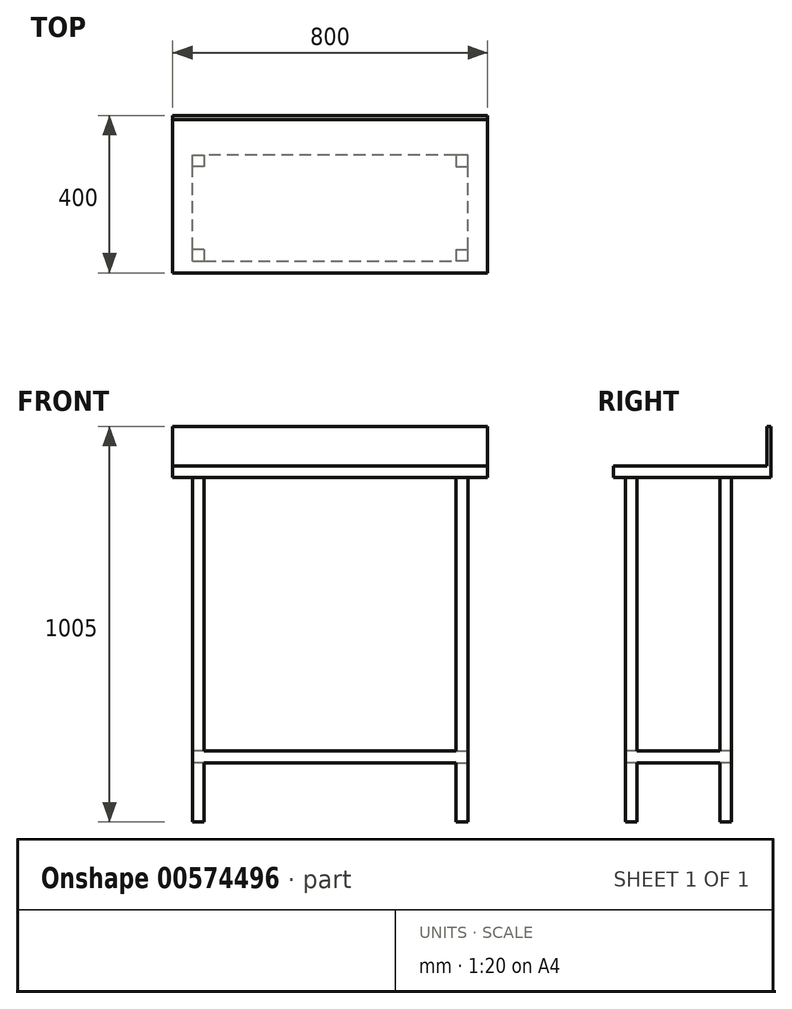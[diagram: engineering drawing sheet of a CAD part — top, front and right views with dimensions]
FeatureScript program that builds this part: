
annotation { "Feature Type Name" : "Feature", "Feature Type Description" : "" }
export const myFeature = defineFeature(function(context is Context, id is Id, definition is map)
    precondition{}
    {
        {
            var Q0;
            Q0=qCreatedBy(makeId("Top.planeOp"),FACE);
            var sketch = newSketch(context, id + "F0", { "sketchPlane" : qUnion([Q0])});
            skLineSegment(sketch, "E0.bottom", {"start": v(400, 200) * mm, "end": v(-400, 200) * mm});
            skLineSegment(sketch, "E0.top", {"start": v(400, -200) * mm, "end": v(-400, -200) * mm});
            skLineSegment(sketch, "E0.left", {"start": v(400, 200) * mm, "end": v(400, -200) * mm});
            skLineSegment(sketch, "E0.right", {"start": v(-400, 200) * mm, "end": v(-400, -200) * mm});
            skPoint(sketch, "E0.middle", {"position": v(0, 0) * mm});
            skSolve(sketch);
        }
        {
            var Q0;
            Q0 = qSketchRegion(id + "F0", true);
            extrude(context, id + "F1", {"entities" : qUnion([Q0]), "depth" : 30 * mm, "offsetDistance" : 25 * mm});
        }
        {
            var Q0;
            Q0=makeQuery(id+"F1.opExtrude","CAP_FACE",FACE,{"disambiguationData":[OSD([sQuery(id+"F0.wireOp",EDGE,"E0.bottom"),sQuery(id+"F0.wireOp",EDGE,"E0.top"),sQuery(id+"F0.wireOp",EDGE,"E0.left"),sQuery(id+"F0.wireOp",EDGE,"E0.right")])],"isStart":false});
            var sketch = newSketch(context, id + "F2", { "sketchPlane" : qUnion([Q0])});
            skLineSegment(sketch, "E1.bottom", {"start": v(-400, 200) * mm, "end": v(400, 200) * mm});
            skLineSegment(sketch, "E1.top", {"start": v(-400, 190) * mm, "end": v(400, 190) * mm});
            skLineSegment(sketch, "E1.left", {"start": v(-400, 200) * mm, "end": v(-400, 190) * mm});
            skLineSegment(sketch, "E1.right", {"start": v(400, 200) * mm, "end": v(400, 190) * mm});
            skSolve(sketch);
        }
        {
            var Q0;
            Q0 = qSketchRegion(id + "F2", true);
            extrude(context, id + "F3", {"entities" : qUnion([Q0]), "operationType" : NewBodyOperationType.ADD, "depth" : 100 * mm, "offsetDistance" : 25 * mm});
        }
        {
            var Q0;
            Q0=makeQuery(id+"F1.opExtrude","CAP_FACE",FACE,{"disambiguationData":[OSD([sQuery(id+"F0.wireOp",EDGE,"E0.bottom"),sQuery(id+"F0.wireOp",EDGE,"E0.top"),sQuery(id+"F0.wireOp",EDGE,"E0.left"),sQuery(id+"F0.wireOp",EDGE,"E0.right")])],"isStart":true});
            var sketch = newSketch(context, id + "F4", { "sketchPlane" : qUnion([Q0])});
            skLineSegment(sketch, "E2.bottom", {"start": v(350, 170) * mm, "end": v(320, 170) * mm});
            skLineSegment(sketch, "E2.top", {"start": v(350, 140) * mm, "end": v(320, 140) * mm});
            skLineSegment(sketch, "E2.left", {"start": v(350, 170) * mm, "end": v(350, 140) * mm});
            skLineSegment(sketch, "E2.right", {"start": v(320, 170) * mm, "end": v(320, 140) * mm});
            skLineSegment(sketch, "E3.bottom", {"start": v(350, -70) * mm, "end": v(320, -70) * mm});
            skLineSegment(sketch, "E3.top", {"start": v(350, -100) * mm, "end": v(320, -100) * mm});
            skLineSegment(sketch, "E3.left", {"start": v(350, -70) * mm, "end": v(350, -100) * mm});
            skLineSegment(sketch, "E3.right", {"start": v(320, -70) * mm, "end": v(320, -100) * mm});
            skLineSegment(sketch, "E4.bottom", {"start": v(-350, 170) * mm, "end": v(-320, 170) * mm});
            skLineSegment(sketch, "E4.top", {"start": v(-350, 140) * mm, "end": v(-320, 140) * mm});
            skLineSegment(sketch, "E4.left", {"start": v(-350, 170) * mm, "end": v(-350, 140) * mm});
            skLineSegment(sketch, "E4.right", {"start": v(-320, 170) * mm, "end": v(-320, 140) * mm});
            skLineSegment(sketch, "E5.bottom", {"start": v(-350, -70) * mm, "end": v(-320, -70) * mm});
            skLineSegment(sketch, "E5.top", {"start": v(-350, -100) * mm, "end": v(-320, -100) * mm});
            skLineSegment(sketch, "E5.left", {"start": v(-350, -70) * mm, "end": v(-350, -100) * mm});
            skLineSegment(sketch, "E5.right", {"start": v(-320, -70) * mm, "end": v(-320, -100) * mm});
            skSolve(sketch);
        }
        {
            var Q0;
            Q0 = qSketchRegion(id + "F4", true);
            extrude(context, id + "F5", {"entities" : qUnion([Q0]), "operationType" : NewBodyOperationType.ADD, "depth" : (905 - 30) * mm, "offsetDistance" : 25 * mm});
        }
        {
            var Q0;
            Q0=qCreatedBy(makeId("Front.planeOp"),FACE);
            var sketch = newSketch(context, id + "F6", { "sketchPlane" : qUnion([Q0])});
            skLineSegment(sketch, "E6.bottom", {"start": v(-350, -695) * mm, "end": v(350, -695) * mm});
            skLineSegment(sketch, "E6.top", {"start": v(-350, -725) * mm, "end": v(350, -725) * mm});
            skLineSegment(sketch, "E6.left", {"start": v(-350, -695) * mm, "end": v(-350, -725) * mm});
            skLineSegment(sketch, "E6.right", {"start": v(350, -695) * mm, "end": v(350, -725) * mm});
            skSolve(sketch);
        }
        {
            var Q0;
            Q0 = qSketchRegion(id + "F6", true);
            var Q1;
            Q1=makeQuery(id+"F5.opExtrude","SWEPT_FACE",FACE,{"disambiguationData":[OSD([sQuery(id+"F4.wireOp",EDGE,"E4.bottom")])]});
            var Q2;
            Q2=makeQuery(id+"F5.opExtrude","SWEPT_FACE",FACE,{"disambiguationData":[OSD([sQuery(id+"F4.wireOp",EDGE,"E3.top")])]});
            extrude(context, id + "F7", {"entities" : qUnion([Q0]), "operationType" : NewBodyOperationType.ADD, "endBound" : BoundingType.UP_TO_SURFACE, "depth" : 25 * mm, "endBoundEntityFace" : qUnion([Q1]), "offsetDistance" : 25 * mm, "hasSecondDirection" : true, "secondDirectionBound" : SecondDirectionBoundingType.UP_TO_SURFACE, "secondDirectionOppositeDirection" : true, "secondDirectionDepth" : 25 * mm, "secondDirectionBoundEntityFace" : qUnion([Q2])});
        }
    });
